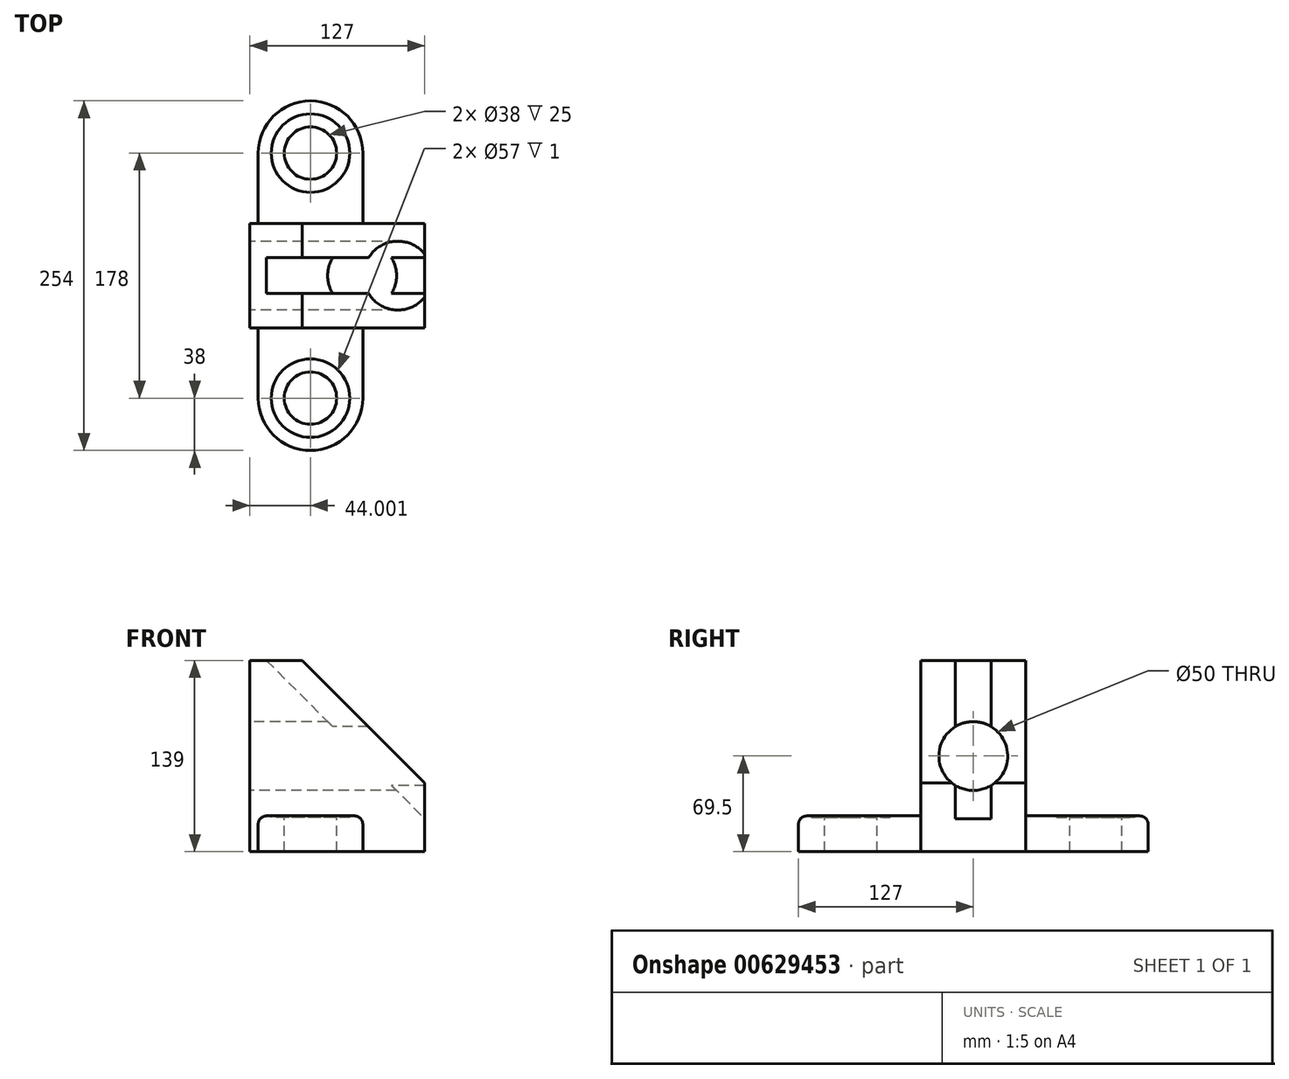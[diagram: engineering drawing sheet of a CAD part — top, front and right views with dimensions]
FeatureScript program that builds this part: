
annotation { "Feature Type Name" : "Feature", "Feature Type Description" : "" }
export const myFeature = defineFeature(function(context is Context, id is Id, definition is map)
    precondition{}
    {
        {
            var Q0;
            Q0=qCreatedBy(makeId("Front.planeOp"),FACE);
            var sketch = newSketch(context, id + "F0", { "sketchPlane" : qUnion([Q0])});
            skLineSegment(sketch, "E0", {"start": v(-60.14, 0) * mm, "end": v(66.86, 0) * mm});
            skLineSegment(sketch, "E1", {"start": v(66.86, 0) * mm, "end": v(66.86, 50) * mm});
            skLineSegment(sketch, "E2", {"start": v(66.86, 50) * mm, "end": v(-22.14, 139) * mm});
            skLineSegment(sketch, "E3", {"start": v(-22.14, 139) * mm, "end": v(-60.14, 139) * mm});
            skLineSegment(sketch, "E4", {"start": v(-60.14, 139) * mm, "end": v(-60.14, 0) * mm});
            skLineSegment(sketch, "E5", {"start": v(66.86, 50) * mm, "end": v(23.84, 50) * mm, "construction": true});
            skSolve(sketch);
        }
        {
            var Q0;
            Q0=makeQuery(id+"F0.imprint","IMPRINT",FACE,{"disambiguationData":[TD([[makeQuery(id+"F0.imprint","IMPRINT",EDGE,{"derivedFrom":sQuery(id+"F0.wireOp",EDGE,"E0")}),1.0]])]});
            extrude(context, id + "F1", {"entities" : qUnion([Q0]), "depth" : (76 / 2) * mm, "offsetDistance" : 25 * mm});
        }
        {
            var Q0;
            Q0=makeQuery(id+"F1.opExtrude","CAP_FACE",FACE,{"disambiguationData":[OSD([sQuery(id+"F0.wireOp",EDGE,"E0"),sQuery(id+"F0.wireOp",EDGE,"E1"),sQuery(id+"F0.wireOp",EDGE,"E2"),sQuery(id+"F0.wireOp",EDGE,"E3"),sQuery(id+"F0.wireOp",EDGE,"E4")])],"isStart":true});
            var sketch = newSketch(context, id + "F2", { "sketchPlane" : qUnion([Q0])});
            skLineSegment(sketch, "E6", {"start": v(48.14, 139) * mm, "end": v(-66.86, 24) * mm});
            skLineSegment(sketch, "E7", {"start": v(48.14, 139) * mm, "end": v(22.14, 139) * mm});
            skLineSegment(sketch, "E8", {"start": v(22.14, 139) * mm, "end": v(-66.86, 50) * mm});
            skLineSegment(sketch, "E9", {"start": v(-66.86, 50) * mm, "end": v(-66.86, 24) * mm});
            skSolve(sketch);
        }
        {
            var Q0;
            Q0 = qSketchRegion(id + "F2", true);
            extrude(context, id + "F3", {"entities" : qUnion([Q0]), "operationType" : NewBodyOperationType.REMOVE, "oppositeDirection" : true, "depth" : (26 / 2) * mm, "offsetDistance" : 25 * mm});
        }
        {
            var Q0;
            Q0=qCreatedBy(makeId("Top.planeOp"),FACE);
            var sketch = newSketch(context, id + "F4", { "sketchPlane" : qUnion([Q0])});
            skLineSegment(sketch, "E10.0", {"start": v(-60.14, -38) * mm, "end": v(66.86, -38) * mm});
            skLineSegment(sketch, "E11", {"start": v(-54.14, -38) * mm, "end": v(-54.14, -89) * mm});
            skLineSegment(sketch, "E12", {"start": v(-54.14, -89) * mm, "end": v(21.86, -89) * mm, "construction": true});
            skLineSegment(sketch, "E13", {"start": v(21.86, -89) * mm, "end": v(21.86, -38) * mm});
            skLineSegment(sketch, "E14", {"start": v(21.86, -38) * mm, "end": v(-54.14, -38) * mm});
            skArc(sketch, "E15", {"start": v(-54.14, -89) * mm, "mid": v(-16.14, -127) * mm, "end": v(21.86, -89) * mm});
            skSolve(sketch);
        }
        {
            var Q0;
            {var subQ0=sQuery(id+"F4.wireOp",EDGE,"E11");Q0=makeQuery(id+"F4.imprint","IMPRINT",FACE,{"disambiguationData":[TD([[makeQuery(id+"F4.imprint","IMPRINT",EDGE,{"derivedFrom":subQ0}),1.0]])]});}
            extrude(context, id + "F5", {"entities" : qUnion([Q0]), "operationType" : NewBodyOperationType.ADD, "depth" : 26 * mm, "offsetDistance" : 25 * mm});
        }
        {
            var Q0;
            Q0=makeQuery(id+"F5.opExtrude","CAP_FACE",FACE,{"disambiguationData":[OSD([sQuery(id+"F4.wireOp",EDGE,"E10.0"),sQuery(id+"F4.wireOp",EDGE,"E11"),sQuery(id+"F4.wireOp",EDGE,"E13"),sQuery(id+"F4.wireOp",EDGE,"E15")])],"isStart":false});
            var sketch = newSketch(context, id + "F6", { "sketchPlane" : qUnion([Q0])});
            skPoint(sketch, "E16.0", {"position": v(-16.14, -89) * mm});
            skCircle(sketch, "E17", {"center": v(-16.14, -89) * mm, "radius": 28.5 * mm});
            skCircle(sketch, "E18", {"center": v(-16.14, -89) * mm, "radius": 19 * mm});
            skSolve(sketch);
        }
        {
            var Q0;
            Q0=makeQuery(id+"F6.imprint","IMPRINT",FACE,{"disambiguationData":[TD([[makeQuery(id+"F6.imprint","IMPRINT",EDGE,{"derivedFrom":sQuery(id+"F6.wireOp",EDGE,"E18")}),1.0]])]});
            extrude(context, id + "F7", {"entities" : qUnion([Q0]), "operationType" : NewBodyOperationType.REMOVE, "endBound" : BoundingType.THROUGH_ALL, "oppositeDirection" : true, "depth" : 25 * mm, "offsetDistance" : 25 * mm});
        }
        {
            var Q0;
            Q0=makeQuery(id+"F6.imprint","IMPRINT",FACE,{"disambiguationData":[TD([[makeQuery(id+"F6.imprint","IMPRINT",EDGE,{"derivedFrom":sQuery(id+"F6.wireOp",EDGE,"E17")}),1.0]])]});
            extrude(context, id + "F8", {"entities" : qUnion([Q0]), "operationType" : NewBodyOperationType.REMOVE, "oppositeDirection" : true, "depth" : 1 * mm, "offsetDistance" : 25 * mm});
        }
        {
            var Q0;
            Q0=makeQuery(id+"F5.opExtrude","CAP_EDGE",EDGE,{"disambiguationData":[OSD([sQuery(id+"F4.wireOp",EDGE,"E10.0")])],"isStart":false});
            var Q1;
            Q1=makeQuery(id+"F5.opExtrude","SWEPT_EDGE",EDGE,{"disambiguationData":[OSD([sQuery(id+"F4.wireOp",EDGE,"E10.0"),sQuery(id+"F4.wireOp",EDGE,"E13")])]});
            var Q2;
            Q2=makeQuery(id+"F5.opExtrude","SWEPT_EDGE",EDGE,{"disambiguationData":[OSD([sQuery(id+"F4.wireOp",EDGE,"E10.0"),sQuery(id+"F4.wireOp",EDGE,"E11")])]});
            var Q3;
            Q3=makeQuery(id+"F5.opExtrude","CAP_EDGE",EDGE,{"disambiguationData":[OSD([sQuery(id+"F4.wireOp",EDGE,"E11")])],"isStart":false});
            fillet(context, id + "F9", {"entities" : qUnion([Q0, Q1, Q2, Q3]), "radius" : 6 * mm, "tangentPropagation" : true, "allowEdgeOverflow" : false});
        }
        {
            var Q0;
            Q0=makeQuery(id+"F1.opExtrude","SWEPT_BODY",BODY,{"disambiguationData":[OSD([sQuery(id+"F0.wireOp",EDGE,"E0"),sQuery(id+"F0.wireOp",EDGE,"E1"),sQuery(id+"F0.wireOp",EDGE,"E2"),sQuery(id+"F0.wireOp",EDGE,"E3"),sQuery(id+"F0.wireOp",EDGE,"E4")])]});
            var Q1;
            Q1=qCreatedBy(makeId("Front.planeOp"),FACE);
            mirror(context, id + "F10", {"operationType" : NewBodyOperationType.ADD, "entities" : qUnion([Q0]), "mirrorPlane" : qUnion([Q1])});
        }
        {
            var Q0;
            {var subQ0=makeQuery(id+"F1.opExtrude","SWEPT_FACE",FACE,{"disambiguationData":[OSD([sQuery(id+"F0.wireOp",EDGE,"E4")])]});Q0=makeQuery(id+"F10.boolean.opBoolean","MERGE",FACE,{"derivedFrom":[subQ0,makeQuery(id+"F10.opPattern","COPY",FACE,{"derivedFrom":subQ0,"instanceName":"1"})]});}
            var sketch = newSketch(context, id + "F11", { "sketchPlane" : qUnion([Q0])});
            skCircle(sketch, "E19", {"center": v(0, 69.5) * mm, "radius": 25 * mm});
            skPoint(sketch, "E19.centerSnap0", {"position": v(0, 139) * mm});
            skLineSegment(sketch, "E20", {"start": v(0, 139) * mm, "end": v(0, 0) * mm, "construction": true});
            skSolve(sketch);
        }
        {
            var Q0;
            Q0=makeQuery(id+"F11.imprint","IMPRINT",FACE,{"disambiguationData":[TD([[makeQuery(id+"F11.imprint","IMPRINT",EDGE,{"derivedFrom":sQuery(id+"F11.wireOp",EDGE,"E19")}),1.0]])]});
            var Q1;
            Q1=sQuery(id+"F11.wireOp",EDGE,"E19");
            extrude(context, id + "F12", {"entities" : qUnion([Q0]), "operationType" : NewBodyOperationType.REMOVE, "surfaceEntities" : qUnion([Q1]), "endBound" : BoundingType.THROUGH_ALL, "oppositeDirection" : true, "depth" : 25 * mm, "offsetDistance" : 25 * mm});
        }
    });
